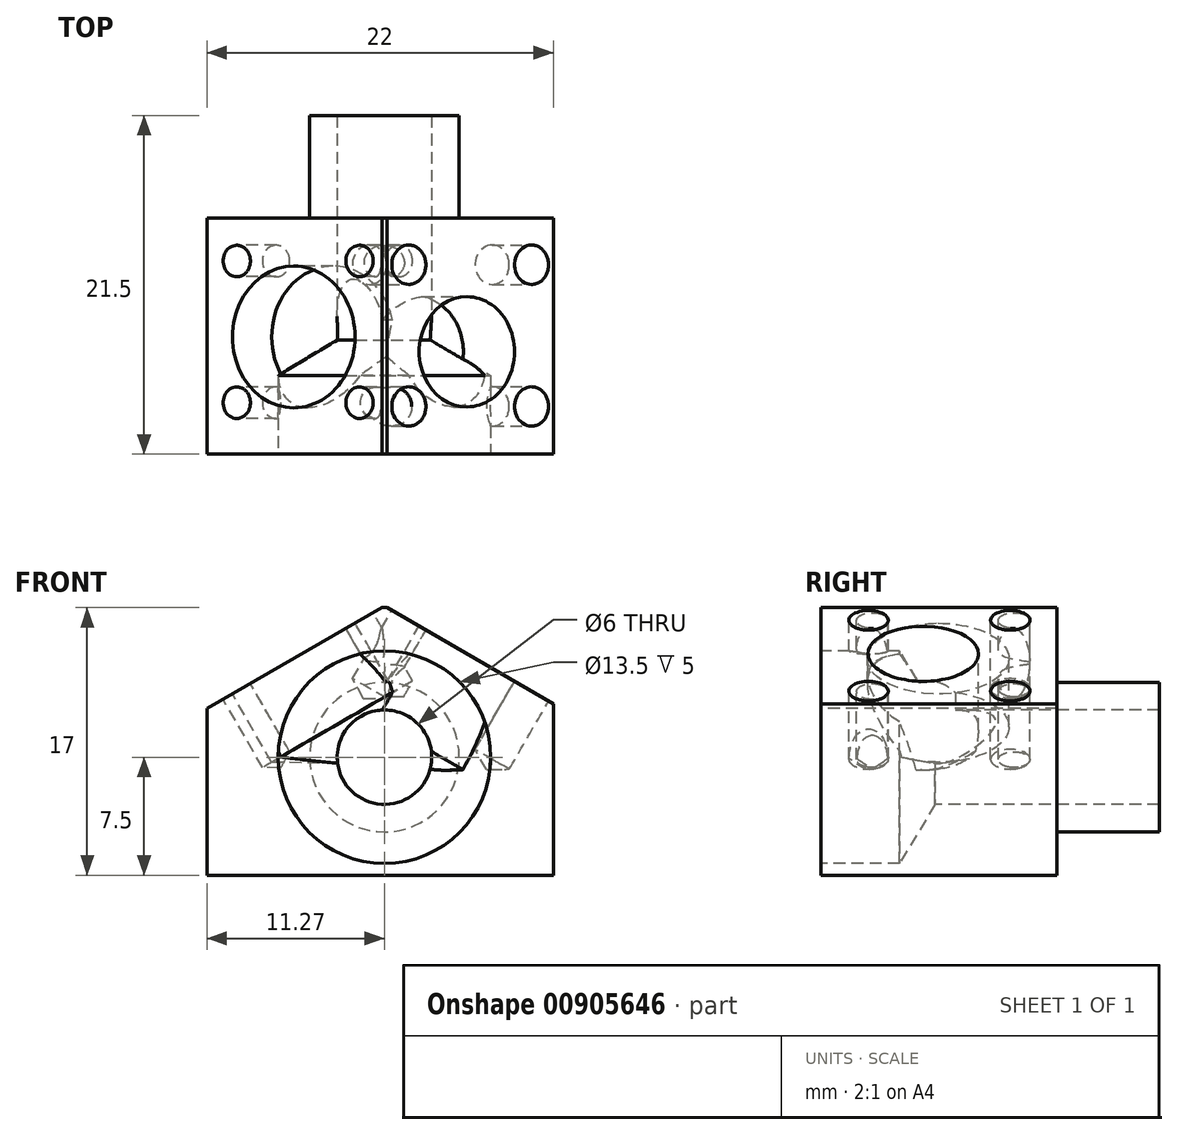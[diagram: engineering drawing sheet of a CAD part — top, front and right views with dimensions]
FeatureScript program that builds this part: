
annotation { "Feature Type Name" : "Feature", "Feature Type Description" : "" }
export const myFeature = defineFeature(function(context is Context, id is Id, definition is map)
    precondition{}
    {
        {
            var Q0;
            Q0=qCreatedBy(makeId("Front.planeOp"),FACE);
            var sketch = newSketch(context, id + "F0", { "sketchPlane" : qUnion([Q0])});
            skLineSegment(sketch, "E0.bottom", {"start": v(10.73, 0) * mm, "end": v(-11.27, 0) * mm});
            skLineSegment(sketch, "E0.top", {"start": v(10.73, 17) * mm, "end": v(-11.27, 17) * mm});
            skLineSegment(sketch, "E0.left", {"start": v(10.73, 0) * mm, "end": v(10.73, 17) * mm});
            skLineSegment(sketch, "E0.right", {"start": v(-11.27, 0) * mm, "end": v(-11.27, 17) * mm});
            skPoint(sketch, "E1", {"position": v(-0.27, 0) * mm});
            skPoint(sketch, "E2", {"position": v(0, 0) * mm});
            skSolve(sketch);
        }
        {
            var Q0;
            Q0=makeQuery(id+"F0.imprint","IMPRINT",FACE,{"disambiguationData":[TD([[makeQuery(id+"F0.imprint","IMPRINT",EDGE,{"derivedFrom":sQuery(id+"F0.wireOp",EDGE,"E0.bottom")}),-1.0]])]});
            extrude(context, id + "F1", {"entities" : qUnion([Q0]), "oppositeDirection" : true, "depth" : 15 * mm, "offsetDistance" : 25 * mm});
        }
        {
            var Q0;
            Q0=makeQuery(id+"F1.opExtrude","CAP_FACE",FACE,{"disambiguationData":[OSD([sQuery(id+"F0.wireOp",EDGE,"E0.bottom"),sQuery(id+"F0.wireOp",EDGE,"E0.top"),sQuery(id+"F0.wireOp",EDGE,"E0.left"),sQuery(id+"F0.wireOp",EDGE,"E0.right")])],"isStart":false});
            var sketch = newSketch(context, id + "F2", { "sketchPlane" : qUnion([Q0])});
            skCircle(sketch, "E3", {"center": v(0, 7.5) * mm, "radius": 4.75 * mm});
            skSolve(sketch);
        }
        {
            var Q0;
            Q0 = qSketchRegion(id + "F2", true);
            extrude(context, id + "F3", {"entities" : qUnion([Q0]), "operationType" : NewBodyOperationType.ADD, "depth" : 6.5 * mm, "offsetDistance" : 25 * mm});
        }
        {
            var Q0;
            Q0=makeQuery(id+"F1.opExtrude","CAP_FACE",FACE,{"disambiguationData":[OSD([sQuery(id+"F0.wireOp",EDGE,"E0.bottom"),sQuery(id+"F0.wireOp",EDGE,"E0.top"),sQuery(id+"F0.wireOp",EDGE,"E0.left"),sQuery(id+"F0.wireOp",EDGE,"E0.right")])],"isStart":true});
            var sketch = newSketch(context, id + "F4", { "sketchPlane" : qUnion([Q0])});
            skCircle(sketch, "E4", {"center": v(0, 7.5) * mm, "radius": 3 * mm});
            skSolve(sketch);
        }
        {
            var Q0;
            Q0=makeQuery(id+"F4.imprint","IMPRINT",FACE,{"disambiguationData":[TD([[makeQuery(id+"F4.imprint","IMPRINT",EDGE,{"derivedFrom":sQuery(id+"F4.wireOp",EDGE,"E4")}),1.0]])]});
            extrude(context, id + "F5", {"entities" : qUnion([Q0]), "operationType" : NewBodyOperationType.REMOVE, "endBound" : BoundingType.THROUGH_ALL, "oppositeDirection" : true, "depth" : 25 * mm, "offsetDistance" : 25 * mm});
        }
        {
            var Q0;
            Q0=qCreatedBy(makeId("Front.planeOp"),FACE);
            var sketch = newSketch(context, id + "F6", { "sketchPlane" : qUnion([Q0])});
            skPoint(sketch, "E5", {"position": v(0, 17.1) * mm});
            skLineSegment(sketch, "E6", {"start": v(0, 17.1) * mm, "end": v(10.73, 10.9) * mm});
            skLineSegment(sketch, "E7", {"start": v(0, 17.1) * mm, "end": v(-11.27, 10.58) * mm});
            skLineSegment(sketch, "E8", {"start": v(-11.27, 10.58) * mm, "end": v(-11.27, 17.1) * mm});
            skLineSegment(sketch, "E9", {"start": v(-11.27, 17.1) * mm, "end": v(10.73, 17.1) * mm});
            skLineSegment(sketch, "E10", {"start": v(10.73, 17.1) * mm, "end": v(10.73, 10.9) * mm});
            skSolve(sketch);
        }
        {
            var Q0;
            Q0=makeQuery(id+"F6.imprint","IMPRINT",FACE,{"disambiguationData":[TD([[makeQuery(id+"F6.imprint","IMPRINT",EDGE,{"derivedFrom":sQuery(id+"F6.wireOp",EDGE,"E6")}),1.0]])]});
            extrude(context, id + "F7", {"entities" : qUnion([Q0]), "operationType" : NewBodyOperationType.REMOVE, "endBound" : BoundingType.THROUGH_ALL, "oppositeDirection" : true, "depth" : 25 * mm, "offsetDistance" : 25 * mm});
        }
        {
            var Q0;
            Q0=makeQuery(id+"F7.boolean.opBoolean","COPY",FACE,{"derivedFrom":makeQuery(id+"F7.opExtrude","SWEPT_FACE",FACE,{"disambiguationData":[OSD([sQuery(id+"F6.wireOp",EDGE,"E6")])]})});
            var sketch = newSketch(context, id + "F8", { "sketchPlane" : qUnion([Q0])});
            skLineSegment(sketch, "E11.bottom", {"start": v(-6.76, 3.03) * mm, "end": v(2.24, 3.03) * mm, "construction": true});
            skLineSegment(sketch, "E11.top", {"start": v(-6.76, 12.03) * mm, "end": v(2.24, 12.03) * mm, "construction": true});
            skLineSegment(sketch, "E11.left", {"start": v(-6.76, 3.03) * mm, "end": v(-6.76, 12.03) * mm, "construction": true});
            skLineSegment(sketch, "E11.right", {"start": v(2.24, 3.03) * mm, "end": v(2.24, 12.03) * mm, "construction": true});
            skPoint(sketch, "E12", {"position": v(-6.76, 3.03) * mm});
            skPoint(sketch, "E13", {"position": v(-6.76, 12.03) * mm});
            skPoint(sketch, "E14", {"position": v(2.24, 12.03) * mm});
            skPoint(sketch, "E15", {"position": v(2.24, 3.03) * mm});
            skSolve(sketch);
        }
        {
            var Q0;
            Q0=sQuery(id+"F8.wireOp",VERTEX,"E12");
            var Q1;
            Q1=sQuery(id+"F8.wireOp",VERTEX,"E13");
            var Q2;
            Q2=sQuery(id+"F8.wireOp",VERTEX,"E14");
            var Q3;
            Q3=sQuery(id+"F8.wireOp",VERTEX,"E15");
            var Q4;
            Q4=makeQuery(id+"F1.opExtrude","SWEPT_BODY",BODY,{"disambiguationData":[OSD([sQuery(id+"F0.wireOp",EDGE,"E0.bottom"),sQuery(id+"F0.wireOp",EDGE,"E0.top"),sQuery(id+"F0.wireOp",EDGE,"E0.left"),sQuery(id+"F0.wireOp",EDGE,"E0.right")])]});
            hole(context, id + "F9", {"style" : HoleStyle.SIMPLE, "endStyle" : HoleEndStyle.BLIND, "standardTappedOrClearance" : lookupTablePath({ "standard" : "ISO", "engagement" : "75%", "pitch" : "0.5 mm", "size" : "M3", "type" : "Tapped" }), "standardBlindInLast" : lookupTablePath({ "standard" : "ISO", "engagement" : "75%", "pitch" : "0.5 mm", "size" : "M3", "type" : "Tapped" }), "holeDiameter" : 2.5 * mm, "majorDiameter" : 3 * mm, "showTappedDepth" : true, "holeDepth" : 5 * mm, "isTappedThrough" : true, "tappedDepth" : 3.5 * mm, "tapClearance" : 3, "locations" : qUnion([Q0, Q1, Q2, Q3]), "scope" : qUnion([Q4])});
        }
        {
            var Q0;
            Q0=makeQuery(id+"F7.boolean.opBoolean","COPY",FACE,{"derivedFrom":makeQuery(id+"F7.opExtrude","SWEPT_FACE",FACE,{"disambiguationData":[OSD([sQuery(id+"F6.wireOp",EDGE,"E6")])]})});
            var sketch = newSketch(context, id + "F10", { "sketchPlane" : qUnion([Q0])});
            skCircle(sketch, "E16", {"center": v(-2.5, 6.5) * mm, "radius": 4 * mm});
            skSolve(sketch);
        }
        {
            var Q0;
            Q0=sQuery(id+"F10.wireOp",VERTEX,"E16.center");
            var Q1;
            Q1=makeQuery(id+"F1.opExtrude","SWEPT_BODY",BODY,{"disambiguationData":[OSD([sQuery(id+"F0.wireOp",EDGE,"E0.bottom"),sQuery(id+"F0.wireOp",EDGE,"E0.top"),sQuery(id+"F0.wireOp",EDGE,"E0.left"),sQuery(id+"F0.wireOp",EDGE,"E0.right")])]});
            hole(context, id + "F11", {"style" : HoleStyle.SIMPLE, "endStyle" : HoleEndStyle.BLIND, "holeDiameter" : 7 * mm, "majorDiameter" : 8 * mm, "holeDepth" : 6.5 * mm, "isTappedThrough" : true, "tappedDepth" : 3.5 * mm, "tapClearance" : 3, "locations" : qUnion([Q0]), "scope" : qUnion([Q1])});
        }
        {
            var Q0;
            Q0=makeQuery(id+"F7.boolean.opBoolean","COPY",FACE,{"derivedFrom":makeQuery(id+"F7.opExtrude","SWEPT_FACE",FACE,{"disambiguationData":[OSD([sQuery(id+"F6.wireOp",EDGE,"E7")])]})});
            var sketch = newSketch(context, id + "F12", { "sketchPlane" : qUnion([Q0])});
            skLineSegment(sketch, "E17.bottom", {"start": v(-2.29, 3.27) * mm, "end": v(6.71, 3.27) * mm, "construction": true});
            skLineSegment(sketch, "E17.top", {"start": v(-2.29, 12.27) * mm, "end": v(6.71, 12.27) * mm, "construction": true});
            skLineSegment(sketch, "E17.left", {"start": v(-2.29, 3.27) * mm, "end": v(-2.29, 12.27) * mm, "construction": true});
            skLineSegment(sketch, "E17.right", {"start": v(6.71, 3.27) * mm, "end": v(6.71, 12.27) * mm, "construction": true});
            skPoint(sketch, "E18", {"position": v(-2.29, 3.27) * mm});
            skPoint(sketch, "E19", {"position": v(-2.29, 12.27) * mm});
            skPoint(sketch, "E20", {"position": v(6.71, 12.27) * mm});
            skPoint(sketch, "E21", {"position": v(6.71, 3.27) * mm});
            skSolve(sketch);
        }
        {
            var Q0;
            Q0=sQuery(id+"F12.wireOp",VERTEX,"E18");
            var Q1;
            Q1=sQuery(id+"F12.wireOp",VERTEX,"E19");
            var Q2;
            Q2=sQuery(id+"F12.wireOp",VERTEX,"E20");
            var Q3;
            Q3=sQuery(id+"F12.wireOp",VERTEX,"E21");
            var Q4;
            Q4=makeQuery(id+"F1.opExtrude","SWEPT_BODY",BODY,{"disambiguationData":[OSD([sQuery(id+"F0.wireOp",EDGE,"E0.bottom"),sQuery(id+"F0.wireOp",EDGE,"E0.top"),sQuery(id+"F0.wireOp",EDGE,"E0.left"),sQuery(id+"F0.wireOp",EDGE,"E0.right")])]});
            hole(context, id + "F13", {"style" : HoleStyle.SIMPLE, "endStyle" : HoleEndStyle.BLIND, "holeDiameter" : 2 * mm, "majorDiameter" : 3 * mm, "holeDepth" : 5 * mm, "isTappedThrough" : true, "tappedDepth" : 3.5 * mm, "tapClearance" : 3, "locations" : qUnion([Q0, Q1, Q2, Q3]), "scope" : qUnion([Q4])});
        }
        {
            var Q0;
            Q0=makeQuery(id+"F7.boolean.opBoolean","COPY",FACE,{"derivedFrom":makeQuery(id+"F7.opExtrude","SWEPT_FACE",FACE,{"disambiguationData":[OSD([sQuery(id+"F6.wireOp",EDGE,"E7")])]})});
            var sketch = newSketch(context, id + "F14", { "sketchPlane" : qUnion([Q0])});
            skCircle(sketch, "E22", {"center": v(1.9, 7.44) * mm, "radius": 4.5 * mm});
            skSolve(sketch);
        }
        {
            var Q0;
            Q0=sQuery(id+"F14.wireOp",VERTEX,"E22.center");
            var Q1;
            Q1=makeQuery(id+"F1.opExtrude","SWEPT_BODY",BODY,{"disambiguationData":[OSD([sQuery(id+"F0.wireOp",EDGE,"E0.bottom"),sQuery(id+"F0.wireOp",EDGE,"E0.top"),sQuery(id+"F0.wireOp",EDGE,"E0.left"),sQuery(id+"F0.wireOp",EDGE,"E0.right")])]});
            hole(context, id + "F15", {"style" : HoleStyle.SIMPLE, "endStyle" : HoleEndStyle.BLIND, "standardTappedOrClearance" : lookupTablePath({ "fit" : "Normal", "standard" : "ISO", "size" : "M8", "type" : "Clearance" }), "standardBlindInLast" : lookupTablePath({ "fit" : "Normal", "standard" : "ISO", "size" : "M8", "type" : "Clearance" }), "holeDiameter" : 9 * mm, "majorDiameter" : 5 * mm, "holeDepth" : 5 * mm, "isTappedThrough" : true, "tappedDepth" : 3.5 * mm, "tapClearance" : 3, "locations" : qUnion([Q0]), "scope" : qUnion([Q1])});
        }
        {
            var Q0;
            Q0=makeQuery(id+"F1.opExtrude","CAP_FACE",FACE,{"disambiguationData":[OSD([sQuery(id+"F0.wireOp",EDGE,"E0.bottom"),sQuery(id+"F0.wireOp",EDGE,"E0.top"),sQuery(id+"F0.wireOp",EDGE,"E0.left"),sQuery(id+"F0.wireOp",EDGE,"E0.right")])],"isStart":true});
            var sketch = newSketch(context, id + "F16", { "sketchPlane" : qUnion([Q0])});
            skCircle(sketch, "E23", {"center": v(0, 7.5) * mm, "radius": 6.25 * mm});
            skSolve(sketch);
        }
        {
            var Q0;
            Q0=sQuery(id+"F16.wireOp",VERTEX,"E23.center");
            var Q1;
            Q1=makeQuery(id+"F1.opExtrude","SWEPT_BODY",BODY,{"disambiguationData":[OSD([sQuery(id+"F0.wireOp",EDGE,"E0.bottom"),sQuery(id+"F0.wireOp",EDGE,"E0.top"),sQuery(id+"F0.wireOp",EDGE,"E0.left"),sQuery(id+"F0.wireOp",EDGE,"E0.right")])]});
            hole(context, id + "F17", {"style" : HoleStyle.SIMPLE, "endStyle" : HoleEndStyle.BLIND, "standardTappedOrClearance" : lookupTablePath({ "fit" : "Normal", "standard" : "ISO", "size" : "M12", "type" : "Clearance" }), "standardBlindInLast" : lookupTablePath({ "fit" : "Normal", "standard" : "ISO", "size" : "M12", "type" : "Clearance" }), "holeDiameter" : 13.5 * mm, "majorDiameter" : 5 * mm, "holeDepth" : 5 * mm, "isTappedThrough" : true, "tappedDepth" : 3.5 * mm, "tapClearance" : 3, "locations" : qUnion([Q0]), "scope" : qUnion([Q1])});
        }
    });
